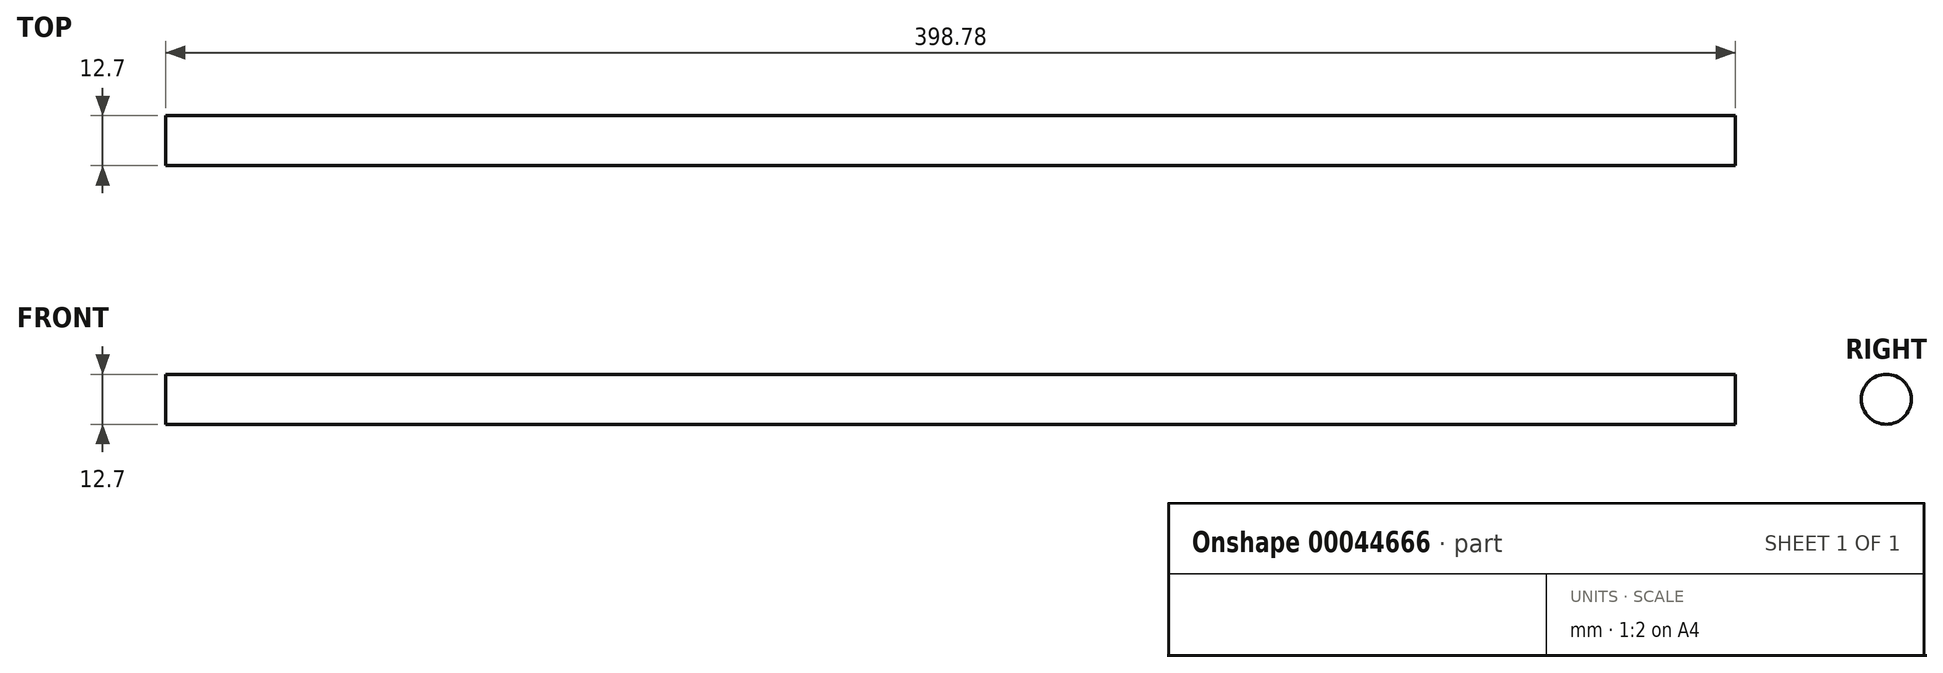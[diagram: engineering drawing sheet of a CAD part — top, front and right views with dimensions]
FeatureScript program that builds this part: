
annotation { "Feature Type Name" : "Feature", "Feature Type Description" : "" }
export const myFeature = defineFeature(function(context is Context, id is Id, definition is map)
    precondition{}
    {
        {
            var Q0;
            Q0=qCreatedBy(makeId("Right.planeOp"),FACE);
            var sketch = newSketch(context, id + "F0", { "sketchPlane" : qUnion([Q0])});
            skCircle(sketch, "E0", {"center": v(0, 0) * mm, "radius": 6.35 * mm});
            skSolve(sketch);
        }
        {
            var Q0;
            Q0=makeQuery(id+"F0.imprint","IMPRINT",FACE,{"disambiguationData":[TD([[makeQuery(id+"F0.imprint","IMPRINT",EDGE,{"derivedFrom":sQuery(id+"F0.wireOp",EDGE,"E0")}),1.0]])]});
            extrude(context, id + "F1", {"entities" : qUnion([Q0]), "oppositeDirection" : true, "depth" : 398.78 * mm});
        }
    });
